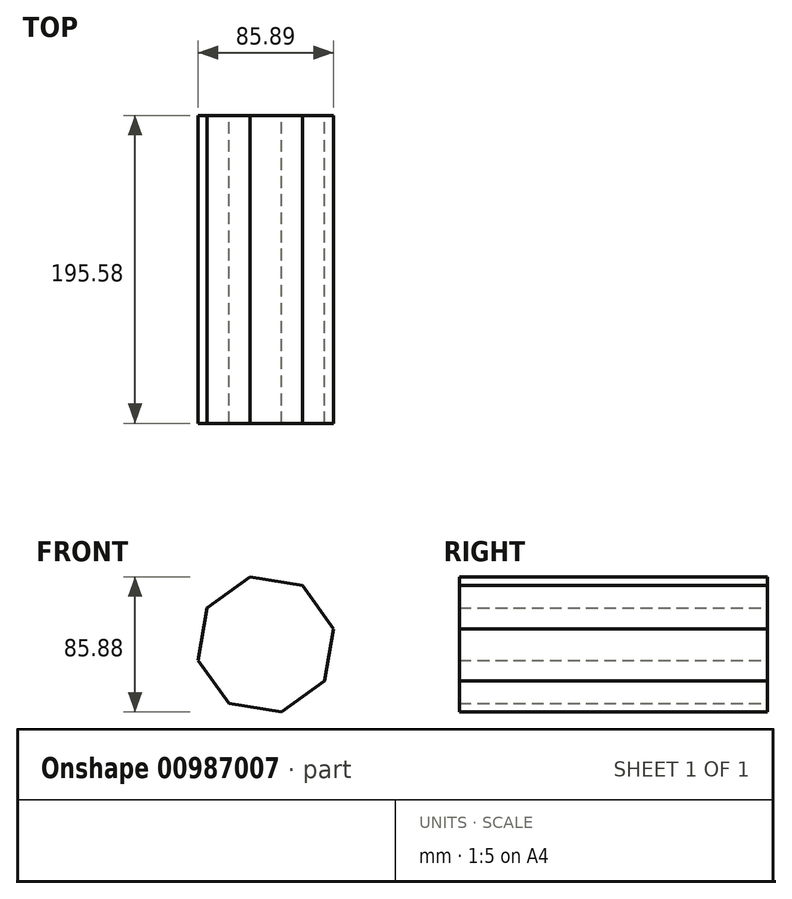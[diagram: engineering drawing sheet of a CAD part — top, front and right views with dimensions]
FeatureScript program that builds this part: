
annotation { "Feature Type Name" : "Feature", "Feature Type Description" : "" }
export const myFeature = defineFeature(function(context is Context, id is Id, definition is map)
    precondition{}
    {
        {
            var Q0;
            Q0=qCreatedBy(makeId("Front.planeOp"),FACE);
            var sketch = newSketch(context, id + "F0", { "sketchPlane" : qUnion([Q0])});
            skCircle(sketch, "E0.cCircle", {"center": v(-121.57, 22.73) * mm, "radius": 40.73 * mm, "construction": true});
            skLineSegment(sketch, "E0.0", {"start": v(-78.62, 32.7) * mm, "end": v(-84.14, -0.58) * mm});
            skLineSegment(sketch, "E0.1", {"start": v(-84.14, -0.58) * mm, "end": v(-111.59, -20.21) * mm});
            skLineSegment(sketch, "E0.2", {"start": v(-111.59, -20.21) * mm, "end": v(-144.88, -14.7) * mm});
            skLineSegment(sketch, "E0.3", {"start": v(-144.88, -14.7) * mm, "end": v(-164.51, 12.75) * mm});
            skLineSegment(sketch, "E0.4", {"start": v(-164.51, 12.75) * mm, "end": v(-158.99, 46.04) * mm});
            skLineSegment(sketch, "E0.5", {"start": v(-158.99, 46.04) * mm, "end": v(-131.55, 65.67) * mm});
            skLineSegment(sketch, "E0.6", {"start": v(-131.55, 65.67) * mm, "end": v(-98.26, 60.15) * mm});
            skLineSegment(sketch, "E0.7", {"start": v(-98.26, 60.15) * mm, "end": v(-78.62, 32.7) * mm});
            skPoint(sketch, "E0.0.midPoint", {"position": v(-81.38, 16.06) * mm});
            skSolve(sketch);
        }
        {
            var Q0;
            Q0=makeQuery(id+"F0.imprint","IMPRINT",FACE,{"disambiguationData":[TD([[makeQuery(id+"F0.imprint","IMPRINT",EDGE,{"derivedFrom":sQuery(id+"F0.wireOp",EDGE,"E0.0")}),-1.0]])]});
            extrude(context, id + "F1", {"entities" : qUnion([Q0]), "depth" : 195.58 * mm, "offsetDistance" : 25.4 * mm});
        }
    });
